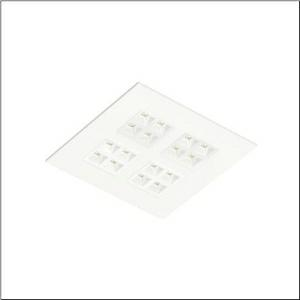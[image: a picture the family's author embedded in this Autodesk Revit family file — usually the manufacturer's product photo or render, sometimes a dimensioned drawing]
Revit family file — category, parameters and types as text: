
# Revit family: silica_r__31_square_51my6nms34wa_c159
name_source: partatom
category: Lighting Fixtures
units: mm (PartAtom-declared; Revit-internal decimal feet)

## family parameters
Cut with Voids When Loaded = No
Host = Face
Light Source = No
Part Type = Normal
Room Calculation Point = No
Round Connector Dimension = Use Diameter
Shared = No

## types (1)
- --- (1 x LED, 6600 lm, 39 W, 3000K)
    Apparent Load = 39 VA
    CIE Flux Codes = 81 99 100 100 100
    Color Rendering = 80
    Color Temperature = 3000K
    Default Elevation = 1800 mm
    Description = Silica® 31 Square, office luminaire, primary light control with lens, of PMMA, primary anti-glare with reflector, of PC, white, light emission: direct distribution, primary light characteristic: symmetric, installation type: lay-in mounting, LED, rated luminous flux: 4.580lm, luminous efficacy: 176lm/W, light colour: 830, colour temperature: 3000K, control gear: ON/OFF Multilumen, with terminal, 3-pole, mains connection: 220..240V, AC, 50/60Hz, rated input power: 26W, luminaire housing, of sheet steel, coated, traffic white (RAL 9016), module: M600, length: 595mm, width: 595mm, height: 43mm, protection rating (complete): IP20, insulation class (complete): insulation class II (safety insulation), certification: CE, impact resistance: IK03, permissible operating ambient temperature: -20..+35°C, standard: EN 50419, packaging unit: 1 piece
    Height = 0 mm  [stored 0 ft]
    Lamp = 1 x LED
    Lamp Light Flux = 6600 lm
    Lamp Power = 39 W
    Lamp count = 1
    Length = 595 mm
    Luminous efficacy = 169 lm/W
    Manufacturer = Siteco
    ModVariant = No
    Model = 51MY6NMS34WA
    Mounting Place = Ceiling
    Mounting Type = Recessed
    Number of Poles = 1
    OnlyDefault = Yes
    Power Factor = 1
    Product Name = Silica® 31 Square
    Product group = office luminaire | ceiling recessed
    ProductGroupID = 401
    Protection Class = Protection class II
    Protection Degree = IP 20
    RLX_Detail_Level = 1
    RLX_Emergency_Light_Flux = 0 lm
    RLX_Emergency_Type = 0
    RLX_Emergency_Type_DB = No
    RlxData = <blob elided: 28541 chars, md5=bc72d821>
    Socket = socket
    Standby Power = 0 W
    System Light Flux = 6600 lm
    System Power = 39 W
    Type Comments = factory setting: luminous flux: 100 % | (ON | ON | ON | ON) | 1100 mA
    Type Image = l_1313651.jpg
    URL = http://relux.com
    VarID = @adj_035974
    Voltage = 0 V
    Weight = 0.00 kg
    Width = 595 mm

note: [stored X ft] marks values corroborated as IEEE doubles in the binary element streams (Revit-internal decimal feet)

## geometry (parser evidence)
native form markers: Blend x4, Sweep x10
no freeform markers — native parametric forms only
